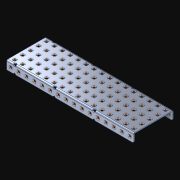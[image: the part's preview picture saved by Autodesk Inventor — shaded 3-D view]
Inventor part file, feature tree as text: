
AUTODESK INVENTOR PART (.ipt)
format: ipt  version: 2021 (Build 250183000, 183)  size: 1,843,712 bytes
history: native  units: in
note: dims shown in document units (in); Inventor stores cm internally (conversion verified against a paired STEP export)
features: extrude x113, other x113, sketch x4, pattern_linear x3
ambient origin geometry x8: Origin, YZ Plane, XZ Plane, XY Plane, X Axis, Y Axis, Z Axis, Center Point
bodies: Solid1 (feature_tree)
feature tree (233):
  pattern_linear  "Rectangular Pattern1"  Spacing1=0.182in  [1 undecoded]
  pattern_linear  "Rectangular Pattern2"  Spacing1=0.046in  [1 undecoded]
  pattern_linear  "Rectangular Pattern3"  Spacing1=0.5in  [1 undecoded]
  extrude  "Extrusion1"  Depth=0.046in
  sketch  "Sketch1"  dims[d0=0.182in]
  other  "Srf1"
  sketch  "Sketch2"  dims[d1=0.046in d2=0.0in]
  other  "Srf2"
  sketch  "Sketch3"  dims[d3=0.182in]
  other  "Srf3"
  other  "Srf4"
  other  "Srf5"
  other  "Srf6"
  other  "Srf7"
  other  "Srf8"
  other  "Srf9"
  other  "Srf10"
  other  "Srf11"
  other  "Srf12"
  other  "Srf13"
  other  "Srf14"
  other  "Srf15"
  other  "Srf16"
  other  "Srf17"
  other  "Srf18"
  other  "Srf38"
  other  "Srf39"
  other  "Srf40"
  other  "Srf41"
  other  "Srf42"
  other  "Srf43"
  other  "Srf44"
  other  "Srf45"
  other  "Srf46"
  other  "Srf47"
  other  "Srf48"
  other  "Srf49"
  other  "Srf50"
  other  "Srf51"
  other  "Srf52"
  other  "Srf72"
  other  "Srf73"
  other  "Srf74"
  other  "Srf75"
  other  "Srf76"
  other  "Srf77"
  other  "Srf78"
  other  "Srf79"
  other  "Srf80"
  other  "Srf81"
  other  "Srf82"
  other  "Srf83"
  other  "Srf84"
  other  "Srf85"
  other  "Srf86"
  other  "Srf87"
  other  "Srf107"
  other  "Srf108"
  other  "Srf109"
  other  "Srf110"
  other  "Srf111"
  other  "Srf112"
  other  "Srf113"
  other  "Srf114"
  other  "Srf115"
  other  "Srf116"
  other  "Srf117"
  other  "Srf118"
  other  "Srf119"
  other  "Srf120"
  other  "Srf121"
  other  "Srf122"
  other  "Srf142"
  other  "Srf143"
  other  "Srf144"
  other  "Srf145"
  other  "Srf146"
  other  "Srf147"
  other  "Srf148"
  other  "Srf149"
  other  "Srf150"
  other  "Srf151"
  other  "Srf152"
  other  "Srf153"
  other  "Srf154"
  other  "Srf155"
  other  "Srf156"
  other  "Srf157"
  other  "Srf177"
  other  "Srf178"
  other  "Srf179"
  other  "Srf180"
  other  "Srf181"
  other  "Srf182"
  other  "Srf183"
  other  "Srf184"
  other  "Srf185"
  other  "Srf186"
  other  "Srf187"
  other  "Srf188"
  other  "Srf189"
  other  "Srf190"
  other  "Srf191"
  other  "Srf192"
  other  "Srf212"
  other  "Srf213"
  other  "Srf214"
  other  "Srf215"
  other  "Srf216"
  other  "Srf217"
  other  "Srf218"
  other  "Srf219"
  other  "Srf220"
  other  "Srf221"
  other  "Srf222"
  other  "Srf223"
  other  "Srf224"
  other  "Srf225"
  other  "Srf226"
  sketch  "Sketch4"  dims[d4=0.046in d5=0.0in d6=0.182in d7=0.046in d8=0.0in d11=0.5in d12=6.2992in d14=0.5in d15=1.9685in d17=0.5in d18=6.2992in d20=0.5in d21=9.5in d22=0.0in]
  parser-record x1  (decoder bookkeeping rows leaked as tree rows — omitted from the tree; the rows remain in map.json)
  extrude  "ExtrusionSrf1"  Depth=0.046in
  extrude  "ExtrusionSrf2"  Depth=0.046in
  extrude  "ExtrusionSrf3"  Depth=0.046in
  extrude  "ExtrusionSrf4"  Depth=0.046in
  extrude  "ExtrusionSrf5"  Depth=0.046in
  extrude  "ExtrusionSrf6"  TaperAngle=0.0deg  [1 undecoded]
  extrude  "ExtrusionSrf7"  [1 undecoded]
  extrude  "ExtrusionSrf8"  [1 undecoded]
  extrude  "ExtrusionSrf9"  [1 undecoded]
  extrude  "ExtrusionSrf10"  [1 undecoded]
  extrude  "ExtrusionSrf11"  [1 undecoded]
  extrude  "ExtrusionSrf12"  [1 undecoded]
  extrude  "ExtrusionSrf13"  [1 undecoded]
  extrude  "ExtrusionSrf14"  [1 undecoded]
  extrude  "ExtrusionSrf15"  [1 undecoded]
  extrude  "ExtrusionSrf16"  [1 undecoded]
  extrude  "ExtrusionSrf17"  [1 undecoded]
  extrude  "ExtrusionSrf18"  [1 undecoded]
  extrude  "ExtrusionSrf38"  [1 undecoded]
  extrude  "ExtrusionSrf39"  [1 undecoded]
  extrude  "ExtrusionSrf40"  [1 undecoded]
  extrude  "ExtrusionSrf41"  [1 undecoded]
  extrude  "ExtrusionSrf42"  [1 undecoded]
  extrude  "ExtrusionSrf43"  [1 undecoded]
  extrude  "ExtrusionSrf44"  [1 undecoded]
  extrude  "ExtrusionSrf45"  [1 undecoded]
  extrude  "ExtrusionSrf46"  [1 undecoded]
  extrude  "ExtrusionSrf47"  [1 undecoded]
  extrude  "ExtrusionSrf48"  [1 undecoded]
  extrude  "ExtrusionSrf49"  [1 undecoded]
  extrude  "ExtrusionSrf50"  [1 undecoded]
  extrude  "ExtrusionSrf51"  [1 undecoded]
  extrude  "ExtrusionSrf52"  [1 undecoded]
  extrude  "ExtrusionSrf72"  [1 undecoded]
  extrude  "ExtrusionSrf73"  [1 undecoded]
  extrude  "ExtrusionSrf74"  [1 undecoded]
  extrude  "ExtrusionSrf75"  [1 undecoded]
  extrude  "ExtrusionSrf76"  [1 undecoded]
  extrude  "ExtrusionSrf77"  [1 undecoded]
  extrude  "ExtrusionSrf78"  [1 undecoded]
  extrude  "ExtrusionSrf79"  [1 undecoded]
  extrude  "ExtrusionSrf80"  [1 undecoded]
  extrude  "ExtrusionSrf81"  [1 undecoded]
  extrude  "ExtrusionSrf82"  [1 undecoded]
  extrude  "ExtrusionSrf83"  [1 undecoded]
  extrude  "ExtrusionSrf84"  [1 undecoded]
  extrude  "ExtrusionSrf85"  [1 undecoded]
  extrude  "ExtrusionSrf86"  [1 undecoded]
  extrude  "ExtrusionSrf87"  [1 undecoded]
  extrude  "ExtrusionSrf107"  [1 undecoded]
  extrude  "ExtrusionSrf108"  [1 undecoded]
  extrude  "ExtrusionSrf109"  [1 undecoded]
  extrude  "ExtrusionSrf110"  [1 undecoded]
  extrude  "ExtrusionSrf111"  [1 undecoded]
  extrude  "ExtrusionSrf112"  [1 undecoded]
  extrude  "ExtrusionSrf113"  [1 undecoded]
  extrude  "ExtrusionSrf114"  [1 undecoded]
  extrude  "ExtrusionSrf115"  [1 undecoded]
  extrude  "ExtrusionSrf116"  [1 undecoded]
  extrude  "ExtrusionSrf117"  [1 undecoded]
  extrude  "ExtrusionSrf118"  [1 undecoded]
  extrude  "ExtrusionSrf119"  [1 undecoded]
  extrude  "ExtrusionSrf120"  [1 undecoded]
  extrude  "ExtrusionSrf121"  [1 undecoded]
  extrude  "ExtrusionSrf122"  [1 undecoded]
  extrude  "ExtrusionSrf142"  [1 undecoded]
  extrude  "ExtrusionSrf143"  [1 undecoded]
  extrude  "ExtrusionSrf144"  [1 undecoded]
  extrude  "ExtrusionSrf145"  [1 undecoded]
  extrude  "ExtrusionSrf146"  [1 undecoded]
  extrude  "ExtrusionSrf147"  [1 undecoded]
  extrude  "ExtrusionSrf148"  [1 undecoded]
  extrude  "ExtrusionSrf149"  [1 undecoded]
  extrude  "ExtrusionSrf150"  [1 undecoded]
  extrude  "ExtrusionSrf151"  [1 undecoded]
  extrude  "ExtrusionSrf152"  [1 undecoded]
  extrude  "ExtrusionSrf153"  [1 undecoded]
  extrude  "ExtrusionSrf154"  [1 undecoded]
  extrude  "ExtrusionSrf155"  [1 undecoded]
  extrude  "ExtrusionSrf156"  [1 undecoded]
  extrude  "ExtrusionSrf157"  [1 undecoded]
  extrude  "ExtrusionSrf177"  [1 undecoded]
  extrude  "ExtrusionSrf178"  [1 undecoded]
  extrude  "ExtrusionSrf179"  [1 undecoded]
  extrude  "ExtrusionSrf180"  [1 undecoded]
  extrude  "ExtrusionSrf181"  [1 undecoded]
  extrude  "ExtrusionSrf182"  [1 undecoded]
  extrude  "ExtrusionSrf183"  [1 undecoded]
  extrude  "ExtrusionSrf184"  [1 undecoded]
  extrude  "ExtrusionSrf185"  [1 undecoded]
  extrude  "ExtrusionSrf186"  [1 undecoded]
  extrude  "ExtrusionSrf187"  [1 undecoded]
  extrude  "ExtrusionSrf188"  [1 undecoded]
  extrude  "ExtrusionSrf189"  [1 undecoded]
  extrude  "ExtrusionSrf190"  [1 undecoded]
  extrude  "ExtrusionSrf191"  [1 undecoded]
  extrude  "ExtrusionSrf192"  [1 undecoded]
  extrude  "ExtrusionSrf212"  [1 undecoded]
  extrude  "ExtrusionSrf213"  [1 undecoded]
  extrude  "ExtrusionSrf214"  [1 undecoded]
  extrude  "ExtrusionSrf215"  [1 undecoded]
  extrude  "ExtrusionSrf216"  [1 undecoded]
  extrude  "ExtrusionSrf217"  [1 undecoded]
  extrude  "ExtrusionSrf218"  [1 undecoded]
  extrude  "ExtrusionSrf219"  [1 undecoded]
  extrude  "ExtrusionSrf220"  [1 undecoded]
  extrude  "ExtrusionSrf221"  [1 undecoded]
  extrude  "ExtrusionSrf222"  [1 undecoded]
  extrude  "ExtrusionSrf223"  [1 undecoded]
  extrude  "ExtrusionSrf224"  [1 undecoded]
  extrude  "ExtrusionSrf225"  [1 undecoded]
  extrude  "ExtrusionSrf226"  [1 undecoded]
note: 110 required parameter values undecoded (feature->parameter linkage not recoverable at this tier; creation-order binding heuristic only, values carry confidence <= 0.55)
